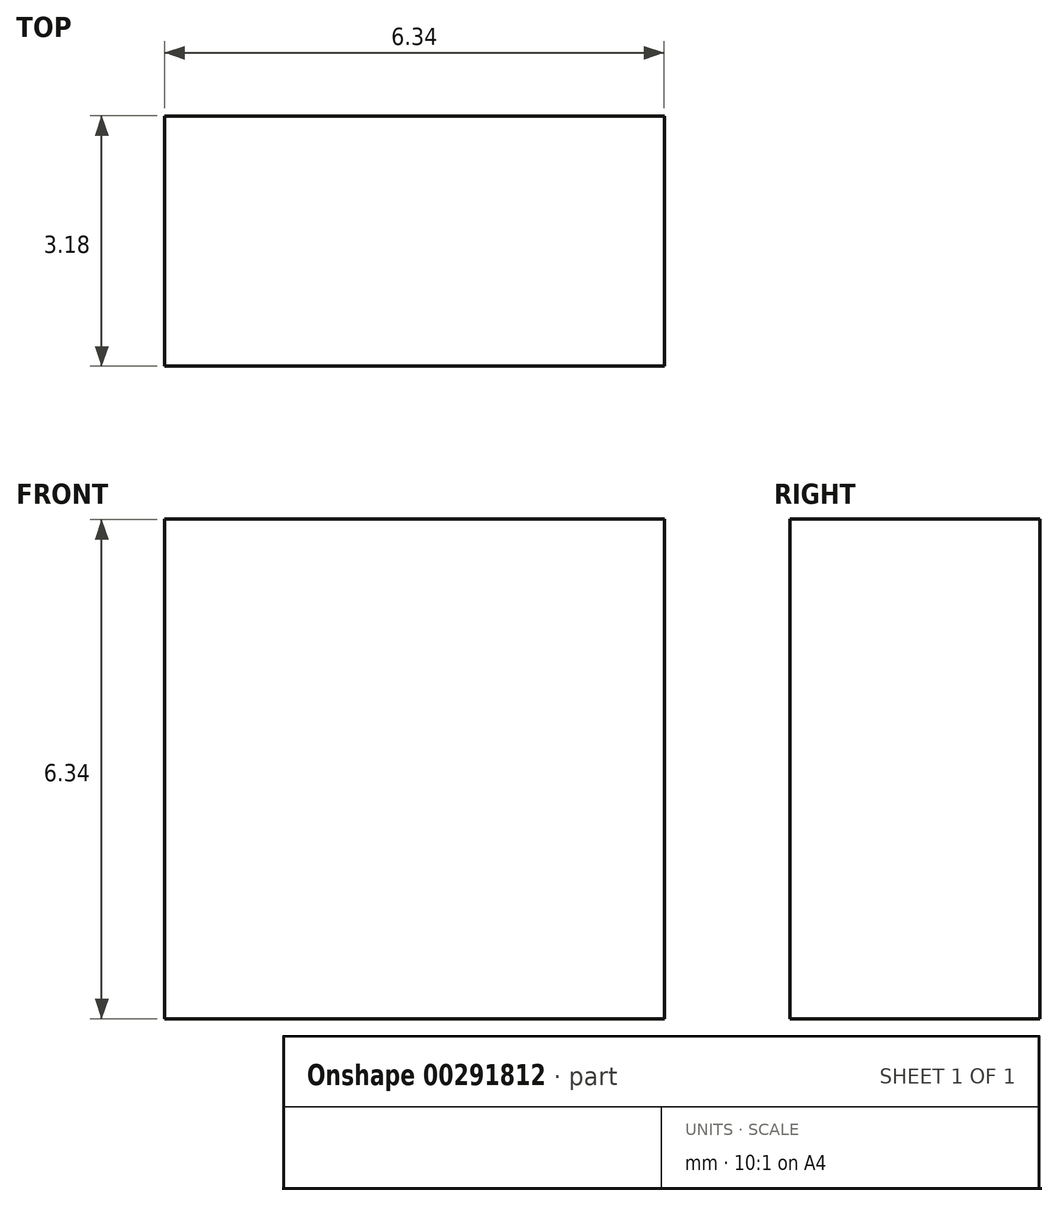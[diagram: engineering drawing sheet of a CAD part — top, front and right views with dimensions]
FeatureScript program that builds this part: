
annotation { "Feature Type Name" : "Feature", "Feature Type Description" : "" }
export const myFeature = defineFeature(function(context is Context, id is Id, definition is map)
    precondition{}
    {
        {
            var Q0;
            Q0=qCreatedBy(makeId("Front.planeOp"),FACE);
            var sketch = newSketch(context, id + "F0", { "sketchPlane" : qUnion([Q0])});
            skLineSegment(sketch, "E0.bottom", {"start": v(3.18, 3.17) * mm, "end": v(-3.17, 3.17) * mm});
            skLineSegment(sketch, "E0.top", {"start": v(3.18, -3.18) * mm, "end": v(-3.18, -3.18) * mm});
            skLineSegment(sketch, "E0.left", {"start": v(3.18, 3.17) * mm, "end": v(3.18, -3.18) * mm});
            skLineSegment(sketch, "E0.right", {"start": v(-3.17, 3.17) * mm, "end": v(-3.18, -3.18) * mm});
            skPoint(sketch, "E0.middle", {"position": v(0, 0) * mm});
            skSolve(sketch);
        }
        {
            var Q0;
            Q0 = qSketchRegion(id + "F0", true);
            extrude(context, id + "F1", {"entities" : qUnion([Q0]), "endBound" : BoundingType.SYMMETRIC, "depth" : 3.17 * mm});
        }
    });
